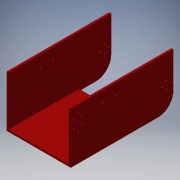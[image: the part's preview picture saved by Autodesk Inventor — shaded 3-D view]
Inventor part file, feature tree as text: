
AUTODESK INVENTOR PART (.ipt)
format: ipt  version: 2016 (Build 200138000, 138)  size: 145,408 bytes
history: native  units: in
note: dims shown in document units (in); Inventor stores cm internally (conversion verified against a paired STEP export)
features: reference x13, sketch x6, extrude x3, hole x3, fillet x1
ambient origin geometry x8: Origin, YZ Plane, XZ Plane, XY Plane, X Axis, Y Axis, Z Axis, Center Point
bodies: Solid1 (feature_tree)
feature tree (26):
  extrude  "Extrusion1"  Depth=8.0in
  extrude  "Extrusion2"  Depth=4.7in
  extrude  "Extrusion3"  Depth=2.5in
  fillet  "Fillet1"  Radius=0.15in
  hole  "Hole1"  [1 undecoded]
  hole  "Hole2"  [1 undecoded]
  hole  "Hole3"  [1 undecoded]
  sketch  "Sketch1"  dims[d0=5.0in d1=8.0in]
  sketch  "Sketch3"  dims[d2=4.0in d3=0.0in d4=4.7in]
  sketch  "Sketch4"  dims[d5=3.85in d6=0.0in d7=2.5in d8=0.15in d9=0.0in]
  sketch  "Sketch6"  dims[d10=1.2in]
  reference  "Reference1"
  reference  "Reference2"
  reference  "Reference3"
  reference  "Reference4"
  reference  "Reference5"
  reference  "Reference6"
  reference  "Reference7"
  sketch  "Sketch7"  dims[d11=0.1457in d12=0.75in d13=0.375in d14=0.25in d15=0.5635in d16=0.15in d17=0.8108in]
  reference  "Reference12"
  reference  "Reference13"
  reference  "Reference14"
  reference  "Reference15"
  sketch  "Sketch8"  dims[d18=0.1457in d19=0.75in d20=0.375in d21=0.25in d22=0.5635in d23=0.15in d24=0.8108in d25=0.1457in d26=0.75in d27=0.375in d28=0.25in d29=0.5635in d30=0.15in d31=0.8108in]
  reference  "Reference16"
  reference  "Reference17"
note: 3 required parameter values undecoded (feature->parameter linkage not recoverable at this tier; creation-order binding heuristic only, values carry confidence <= 0.55)
